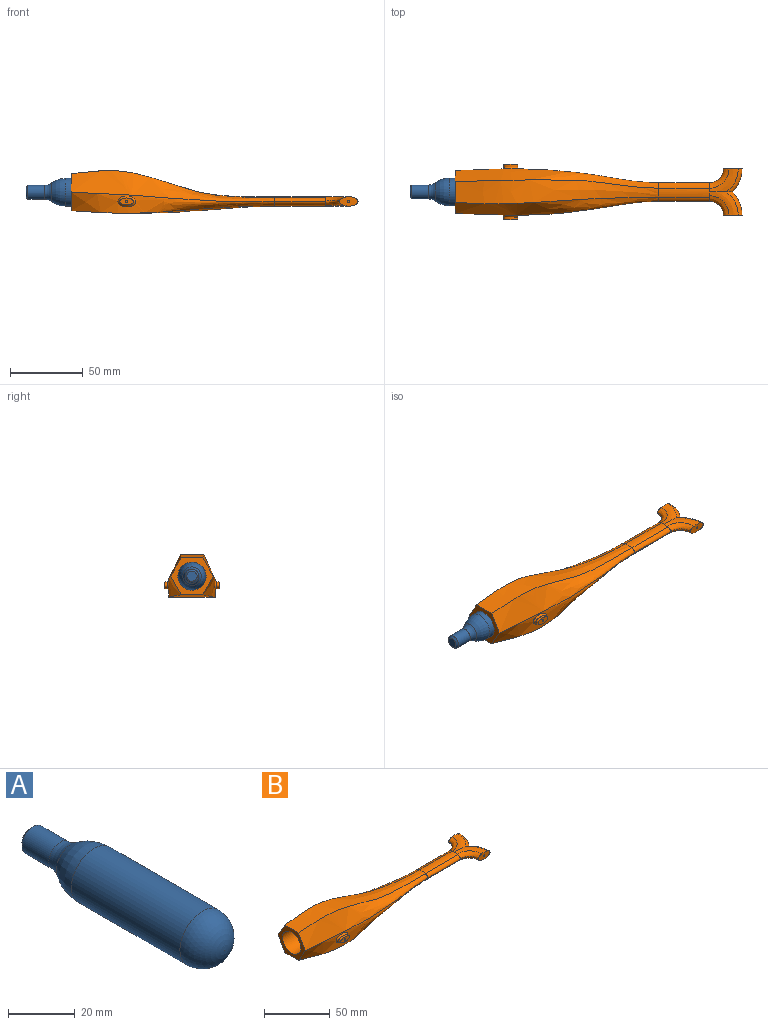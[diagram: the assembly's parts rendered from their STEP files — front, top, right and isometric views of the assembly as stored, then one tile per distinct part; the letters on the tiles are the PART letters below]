
ASSEMBLY  parts=2 mates=1
PART A: 7 faces, bbox 19.1x82.6x19.1 mm
  f0: plane 6.99x6.99mm, normal (0,1,0), area 38.3mm2, adj f6
  f1: cylinder r=4.76mm len=11.43mm, axis (0,1,0), area 342mm2, adj f2,f6
  f2: torus R=12.7mm, axis (0,1,0), area 170.1mm2, adj f1,f3
  f3: revolved ~19.05x19.05mm, area 541.9mm2, adj f2,f4
  f4: cylinder r=9.53mm len=46.05mm, axis (0,1,0), area 2756mm2, adj f3,f5
  f5: sphere r=9.53mm, area 570mm2, adj f4
  f6: cone r=3.49mm half-angle=45deg, axis (0,-1,0), area 46.6mm2, adj f0,f1
PART B: 43 faces, bbox 197.6x43.1x34.6 mm
  f0: bspline ~139.7x18.07mm, area 1301.2mm2, adj f2,f3,f4,f11,f40
  f1: bspline ~139.7x21.63mm, area 1335.5mm2, adj f2,f4,f5,f13,f39
  f2: plane 29.33x25.4mm, normal (-1,0,0), area 263.1mm2, adj f0,f1,f3,f4,f5,f6,f41
  f3: bspline ~139.7x24.45mm, area 1674.2mm2, adj f0,f2,f6,f10
  f4: bspline ~139.7x42.34mm, area 2588.4mm2, adj f0,f1,f2,f12
  f5: bspline ~139.7x27.7mm, area 1623.9mm2, adj f1,f2,f6,f14
  f6: bspline ~139.7x24.63mm, area 1836.7mm2, adj f2,f3,f5,f9
  f7: bspline ~18.47x18.47mm, area 137.1mm2, adj f8,f12,f17,f18,f22
  f8: plane 13.5x7.15mm, normal (0,1,0), area 61.6mm2, adj f7,f15,f16,f17,f18,f19,f20
  f9: bspline ~34.93x6.32mm, area 223.6mm2, adj f6,f10,f14,f15,f24,f28
  f10: bspline ~34.93x2.9mm, area 147.6mm2, adj f3,f9,f11,f27,f28
  f11: bspline ~34.93x3.72mm, area 165.8mm2, adj f0,f10,f12,f22,f27
  f12: bspline ~34.93x6.32mm, area 223.6mm2, adj f4,f7,f11,f13,f22
  f13: bspline ~34.93x2.9mm, area 147.6mm2, adj f1,f12,f14,f18
  f14: bspline ~34.93x3.72mm, area 165.8mm2, adj f5,f9,f13,f19
  f15: bspline ~19.6x19.6mm, area 144.2mm2, adj f8,f9,f16,f19,f24
  f16: bspline ~18x10.74mm, area 78.1mm2, adj f8,f15,f17,f25
  f17: bspline ~22.19x22.19mm, area 89.1mm2, adj f7,f8,f16,f26
  f18: bspline ~12.15x12.15mm, area 69.7mm2, adj f7,f8,f13,f19
  f19: bspline ~13.28x13.28mm, area 83.3mm2, adj f8,f14,f15,f18
  f20: cylinder r=0.75mm len=12.7mm, axis (0,1,0), area 59.8mm2, adj f8,f21
  f21: plane 1.5x1.5mm, normal (0,1,0), area 1.8mm2, adj f20
  f22: bspline ~18.47x18.47mm, area 137.1mm2, adj f7,f11,f12,f23,f26,f27
  f23: plane 13.5x7.15mm, normal (0,-1,0), area 61.6mm2, adj f22,f24,f25,f26,f27,f28,f29
  f24: bspline ~19.6x19.6mm, area 144.2mm2, adj f9,f15,f23,f25,f28
  f25: bspline ~18x10.74mm, area 78.1mm2, adj f16,f23,f24,f26
  f26: bspline ~22.19x22.19mm, area 89.1mm2, adj f17,f22,f23,f25
  f27: bspline ~12.15x12.15mm, area 69.7mm2, adj f10,f11,f22,f23,f28
  f28: bspline ~13.28x13.28mm, area 83.3mm2, adj f9,f10,f23,f24,f27
  f29: cylinder r=0.75mm len=12.7mm, axis (0,-1,0), area 59.8mm2, adj f23,f30
  f30: plane 1.5x1.5mm, normal (0,-1,0), area 1.8mm2, adj f29
  f31: cylinder r=0.75mm len=3.18mm, axis (0,1,0), area 15mm2, adj f32,f34
  f32: plane 9.53x4.76mm, normal (0,1,0), area 33.9mm2, adj f31,f33
  f33: extruded ~9.53x4.76mm, area 45.4mm2, adj f32,f39
  f34: bspline ~122.76x13.63mm, area 1.8mm2, adj f31
  f35: cylinder r=0.75mm len=3.18mm, axis (0,1,0), area 15mm2, adj f37,f38
  f36: extruded ~9.53x4.76mm, area 45.2mm2, adj f37,f40
  f37: plane 9.53x4.76mm, normal (0,-1,0), area 33.9mm2, adj f35,f36
  f38: bspline ~122.76x13.7mm, area 1.8mm2, adj f35
  f39: bspline ~11.92x7.26mm, area 47.3mm2, adj f1,f33
  f40: bspline ~11.94x7.26mm, area 47.5mm2, adj f0,f36
  f41: cylinder r=9.7mm len=50.8mm, axis (1,0,0), area 3096.1mm2, adj f2,f42
  f42: plane 19.4x19.4mm, normal (-1,0,0), area 295.6mm2, adj f41
PLACE A rot(axis=(-0.58,0.58,0.58),120deg) t=(-101.91,15.97,-0.45)mm
PLACE B t=(-32.86,15.97,-6.8)mm
MATE revolute A.f1 <-> B.f41  axis (-1,0,0) through (-51.91,15.97,-0.45)mm
